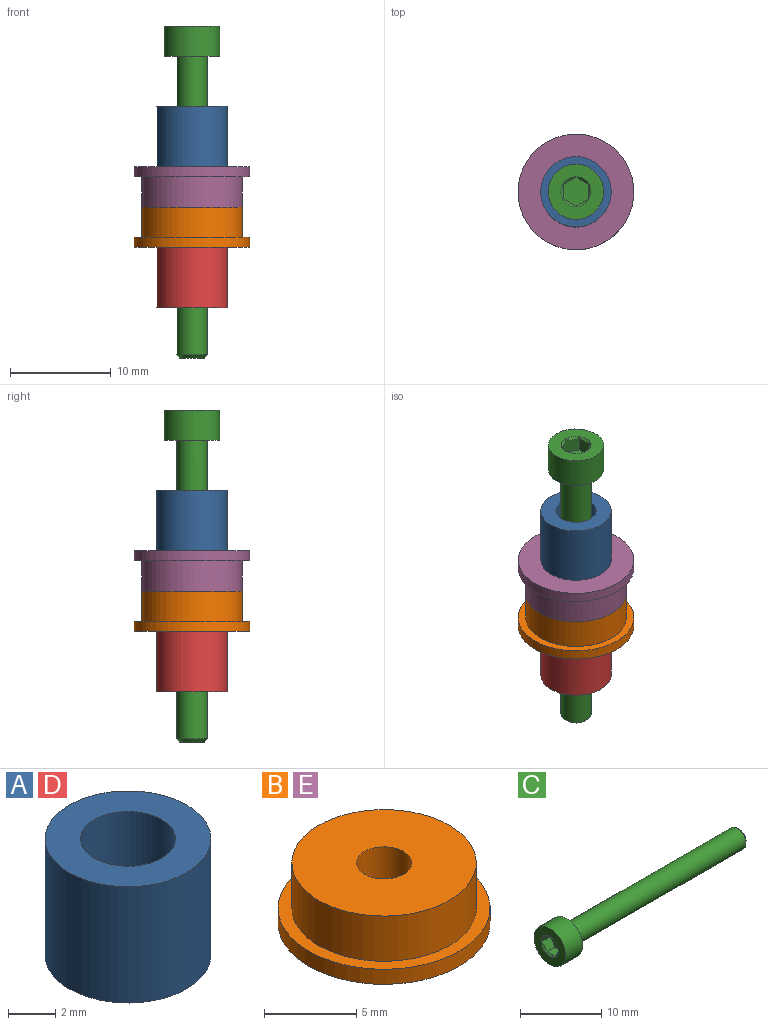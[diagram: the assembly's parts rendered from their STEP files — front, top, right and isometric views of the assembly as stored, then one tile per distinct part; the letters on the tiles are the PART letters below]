
ASSEMBLY  parts=5 mates=4
PART A: 4 faces, bbox 7x7x6 mm
  f0: cylinder r=2mm len=6mm, axis (0,0,-1), area 75.4mm2, adj f2,f3
  f1: cylinder r=3.5mm len=7mm, axis (0,0,-1), area 131.9mm2, adj f2,f3
  f2: plane 7x7mm, normal (0,0,1), area 25.9mm2, adj f0,f1
  f3: plane 7x7mm, normal (0,0,-1), area 25.9mm2, adj f0,f1
PART B: 6 faces, bbox 11.5x11.5x4 mm
  f0: cylinder r=5.75mm len=11.5mm, axis (0,0,-1), area 36.1mm2, adj f1,f2
  f1: plane 11.5x11.5mm, normal (0,0,1), area 25.3mm2, adj f0,f3
  f2: plane 11.5x11.5mm, normal (0,0,-1), area 96.8mm2, adj f0,f4
  f3: cylinder r=5mm len=10mm, axis (0,0,-1), area 94.2mm2, adj f1,f5
  f4: cylinder r=1.5mm len=4mm, axis (0,0,-1), area 37.7mm2, adj f2,f5
  f5: plane 10x10mm, normal (0,0,1), area 71.5mm2, adj f3,f4
PART C: 14 faces, bbox 33x5.5x5.5 mm
  f0: cone r=1.49mm half-angle=45deg, axis (-1,0,0), area 2.3mm2, adj f5,f8,f9,f10,f11,f12,f13
  f1: cylinder r=2.75mm len=5.5mm, axis (-1,0,0), area 51.8mm2, adj f5,f6
  f2: cone r=1.2mm half-angle=45deg, axis (-1,0,0), area 3.6mm2, adj f3,f4
  f3: cylinder r=1.5mm len=29.7mm, axis (1,0,0), area 279.9mm2, adj f2,f6
  f4: plane 2.4x2.4mm, normal (1,0,0), area 4.5mm2, adj f2
  f5: plane 5.5x5.5mm, normal (-1,0,0), area 16.8mm2, adj f0,f1
  f6: plane 5.5x5.5mm, normal (1,0,0), area 16.7mm2, adj f1,f3
  f7: plane 2.89x2.5mm, normal (-1,0,0), area 5.4mm2, adj f8,f9,f10,f11,f12,f13
  f8: plane 1.55x1.25mm, normal (0,-0.87,0.5), area 2.1mm2, adj f0,f7,f9,f13
  f9: plane 1.55x1.44mm, normal (0,0,1), area 2.1mm2, adj f0,f7,f8,f10
  f10: plane 1.55x1.25mm, normal (0,0.87,0.5), area 2.1mm2, adj f0,f7,f9,f11
  f11: plane 1.55x1.25mm, normal (0,0.87,-0.5), area 2.1mm2, adj f0,f7,f10,f12
  f12: plane 1.55x1.44mm, normal (0,0,-1), area 2.1mm2, adj f0,f7,f11,f13
  f13: plane 1.55x1.25mm, normal (0,-0.87,-0.5), area 2.1mm2, adj f0,f7,f8,f12
PART D: same geometry as A
PART E: same geometry as B
PLACE A t=(-18.35,-12.06,6)mm
PLACE B t=(-6.52,-6.3,-2)mm
PLACE C rot(axis=(0.71,0,-0.71),180deg) t=(-6.52,-6.3,-13)mm
PLACE D rot(axis=(1,0,0),180deg) t=(-18.35,-0.55,-2)mm
PLACE E rot(axis=(1,0,0),180deg) t=(-6.52,-6.3,6)mm
MATE fastened E.f0 <-> A.f0  axis (0,0,1) through (-6.52,-6.3,6)mm
MATE fastened E.f0 <-> B.f0  axis (0,0,-1) through (-6.52,-6.3,2)mm
MATE fastened D.f0 <-> B.f0  axis (0,0,1) through (-6.52,-6.3,-2)mm
MATE fastened C.f2 <-> A.f0  axis (0,0,-1) through (-6.52,-6.3,17)mm
